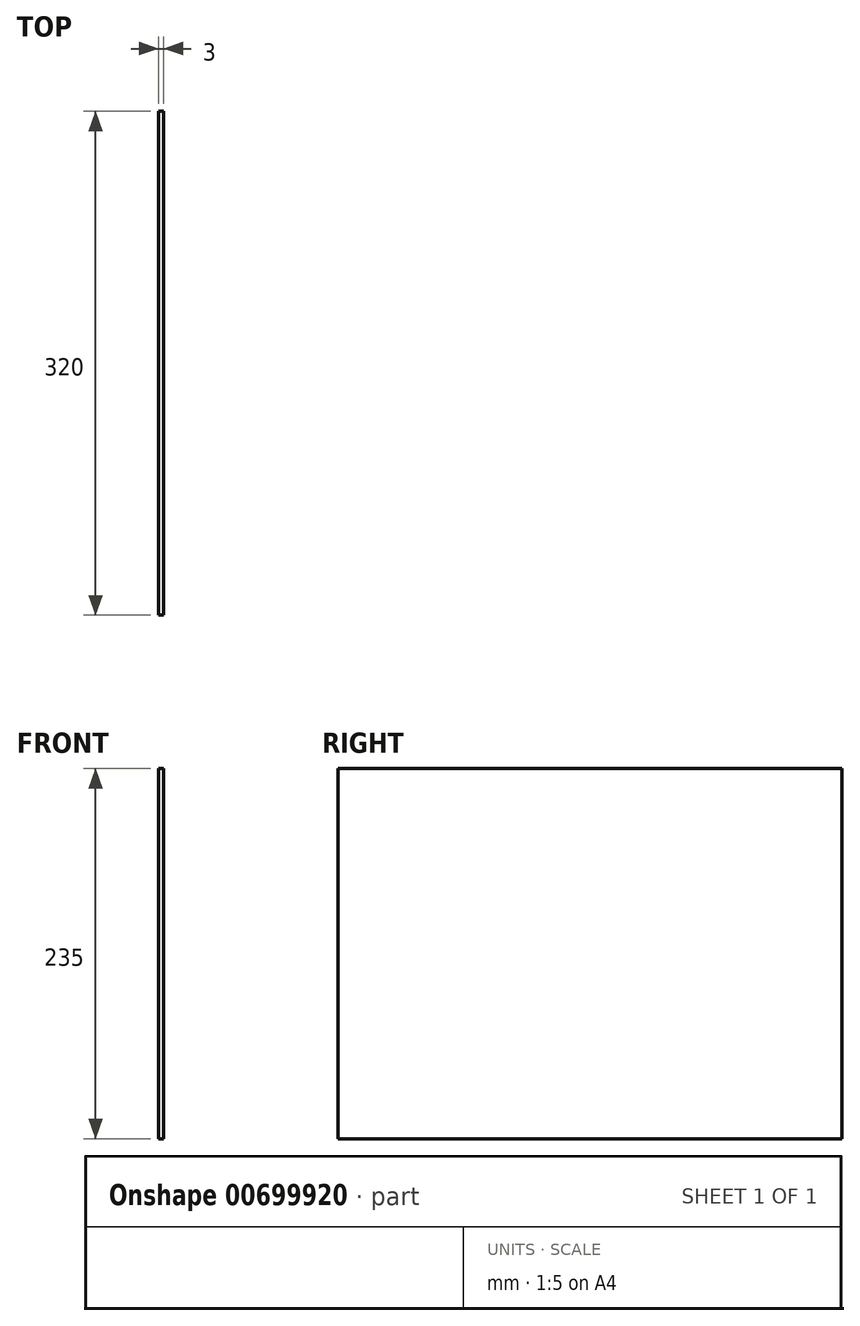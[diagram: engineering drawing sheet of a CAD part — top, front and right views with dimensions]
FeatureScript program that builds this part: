
annotation { "Feature Type Name" : "Feature", "Feature Type Description" : "" }
export const myFeature = defineFeature(function(context is Context, id is Id, definition is map)
    precondition{}
    {
        {
            var Q0;
            Q0=qCreatedBy(makeId("Right.planeOp"),FACE);
            var sketch = newSketch(context, id + "F0", { "sketchPlane" : qUnion([Q0])});
            skLineSegment(sketch, "E0.bottom", {"start": v(0, 0) * mm, "end": v(320, 0) * mm});
            skLineSegment(sketch, "E0.top", {"start": v(0, 235) * mm, "end": v(320, 235) * mm});
            skLineSegment(sketch, "E0.left", {"start": v(0, 0) * mm, "end": v(0, 235) * mm});
            skLineSegment(sketch, "E0.right", {"start": v(320, 0) * mm, "end": v(320, 235) * mm});
            skSolve(sketch);
        }
        {
            var Q0;
            Q0=makeQuery(id+"F0.imprint","IMPRINT",FACE,{"disambiguationData":[TD([[makeQuery(id+"F0.imprint","IMPRINT",EDGE,{"derivedFrom":sQuery(id+"F0.wireOp",EDGE,"E0.bottom")}),1.0]])]});
            extrude(context, id + "F1", {"entities" : qUnion([Q0]), "depth" : 3 * mm, "offsetDistance" : 25 * mm});
        }
    });
